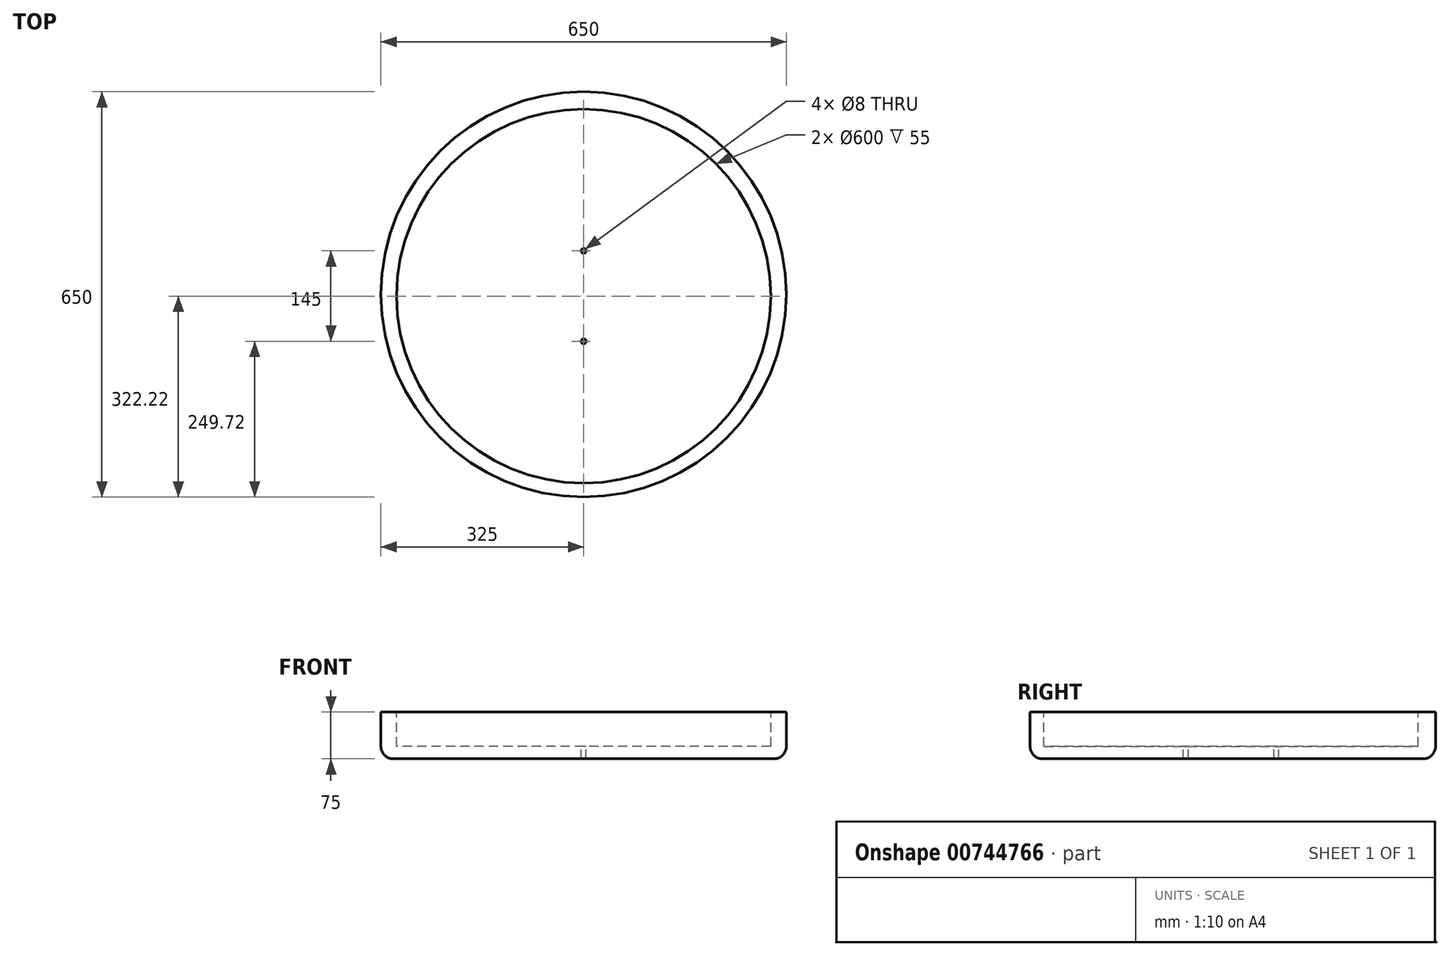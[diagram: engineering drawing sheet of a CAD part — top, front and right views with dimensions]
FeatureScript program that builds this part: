
annotation { "Feature Type Name" : "Feature", "Feature Type Description" : "" }
export const myFeature = defineFeature(function(context is Context, id is Id, definition is map)
    precondition{}
    {
        {
            var Q0;
            Q0=qCreatedBy(makeId("Top.planeOp"),FACE);
            var sketch = newSketch(context, id + "F0", { "sketchPlane" : qUnion([Q0])});
            skCircle(sketch, "E0", {"center": v(0, 2.78) * mm, "radius": 325 * mm});
            skSolve(sketch);
        }
        {
            var Q0;
            Q0=makeQuery(id+"F0.imprint","IMPRINT",FACE,{"disambiguationData":[TD([[makeQuery(id+"F0.imprint","IMPRINT",EDGE,{"derivedFrom":sQuery(id+"F0.wireOp",EDGE,"E0")}),1.0]])]});
            extrude(context, id + "F1", {"entities" : qUnion([Q0]), "depth" : 75 * mm, "offsetDistance" : 25 * mm});
        }
        {
            var Q0;
            Q0=makeQuery(id+"F1.opExtrude","CAP_FACE",FACE,{"disambiguationData":[OSD([sQuery(id+"F0.wireOp",EDGE,"E0")])],"isStart":false});
            var sketch = newSketch(context, id + "F2", { "sketchPlane" : qUnion([Q0])});
            skCircle(sketch, "E1", {"center": v(0, 0) * mm, "radius": 300 * mm});
            skSolve(sketch);
        }
        {
            var Q0;
            Q0=makeQuery(id+"F2.imprint","IMPRINT",FACE,{"disambiguationData":[TD([[makeQuery(id+"F2.imprint","IMPRINT",EDGE,{"derivedFrom":sQuery(id+"F2.wireOp",EDGE,"E1")}),1.0]])]});
            extrude(context, id + "F3", {"entities" : qUnion([Q0]), "operationType" : NewBodyOperationType.REMOVE, "oppositeDirection" : true, "depth" : 55 * mm, "offsetDistance" : 25 * mm});
        }
        {
            var Q0;
            Q0=makeQuery(id+"F1.opExtrude","CAP_EDGE",EDGE,{"disambiguationData":[OSD([sQuery(id+"F0.wireOp",EDGE,"E0")])],"isStart":true});
            fillet(context, id + "F4", {"entities" : qUnion([Q0]), "radius" : 20 * mm, "tangentPropagation" : true, "allowEdgeOverflow" : false});
        }
        {
            var Q0;
            Q0=makeQuery(id+"F3.boolean.opBoolean","COPY",FACE,{"derivedFrom":makeQuery(id+"F3.opExtrude","CAP_FACE",FACE,{"disambiguationData":[OSD([sQuery(id+"F2.wireOp",EDGE,"E1")])],"isStart":false})});
            var sketch = newSketch(context, id + "F5", { "sketchPlane" : qUnion([Q0])});
            skCircle(sketch, "E2", {"center": v(0, 0) * mm, "radius": 72.5 * mm});
            skCircle(sketch, "E3", {"center": v(0, 72.5) * mm, "radius": 4 * mm});
            skCircle(sketch, "E4", {"center": v(0, -72.5) * mm, "radius": 4 * mm});
            skSolve(sketch);
        }
        {
            var Q0;
            {var subQ0=sQuery(id+"F5.wireOp",EDGE,"E3");var subQ1=sQuery(id+"F5.wireOp",EDGE,"E2");var subQ2=makeQuery(id+"F5.imprint","INTERSECT",VERTEX,{"disambiguationData":[OD(0.0)],"derivedFrom":[subQ1,subQ0]});Q0=makeQuery(id+"F5.imprint","IMPRINT",FACE,{"disambiguationData":[TD([[makeQuery(id+"F5.imprint","IMPRINT",EDGE,{"disambiguationData":[TD([[subQ2,1.0]])],"derivedFrom":subQ1}),-1.0]])]});}
            var Q1;
            {var subQ0=sQuery(id+"F5.wireOp",EDGE,"E3");var subQ1=sQuery(id+"F5.wireOp",EDGE,"E2");var subQ2=makeQuery(id+"F5.imprint","INTERSECT",VERTEX,{"disambiguationData":[OD(0.0)],"derivedFrom":[subQ1,subQ0]});Q1=makeQuery(id+"F5.imprint","IMPRINT",FACE,{"disambiguationData":[TD([[makeQuery(id+"F5.imprint","IMPRINT",EDGE,{"disambiguationData":[TD([[subQ2,1.0]])],"derivedFrom":subQ1}),1.0]])]});}
            var Q2;
            {var subQ0=sQuery(id+"F5.wireOp",EDGE,"E4");var subQ1=sQuery(id+"F5.wireOp",EDGE,"E2");var subQ2=makeQuery(id+"F5.imprint","INTERSECT",VERTEX,{"disambiguationData":[OD(0.0)],"derivedFrom":[subQ1,subQ0]});Q2=makeQuery(id+"F5.imprint","IMPRINT",FACE,{"disambiguationData":[TD([[makeQuery(id+"F5.imprint","IMPRINT",EDGE,{"disambiguationData":[TD([[subQ2,-1.0]])],"derivedFrom":subQ1}),-1.0]])]});}
            var Q3;
            {var subQ0=sQuery(id+"F5.wireOp",EDGE,"E4");var subQ1=sQuery(id+"F5.wireOp",EDGE,"E2");var subQ2=makeQuery(id+"F5.imprint","INTERSECT",VERTEX,{"disambiguationData":[OD(0.0)],"derivedFrom":[subQ1,subQ0]});Q3=makeQuery(id+"F5.imprint","IMPRINT",FACE,{"disambiguationData":[TD([[makeQuery(id+"F5.imprint","IMPRINT",EDGE,{"disambiguationData":[TD([[subQ2,-1.0]])],"derivedFrom":subQ1}),1.0]])]});}
            extrude(context, id + "F6", {"entities" : qUnion([Q0, Q1, Q2, Q3]), "operationType" : NewBodyOperationType.REMOVE, "oppositeDirection" : true, "depth" : 25 * mm, "offsetDistance" : 25 * mm});
        }
    });
